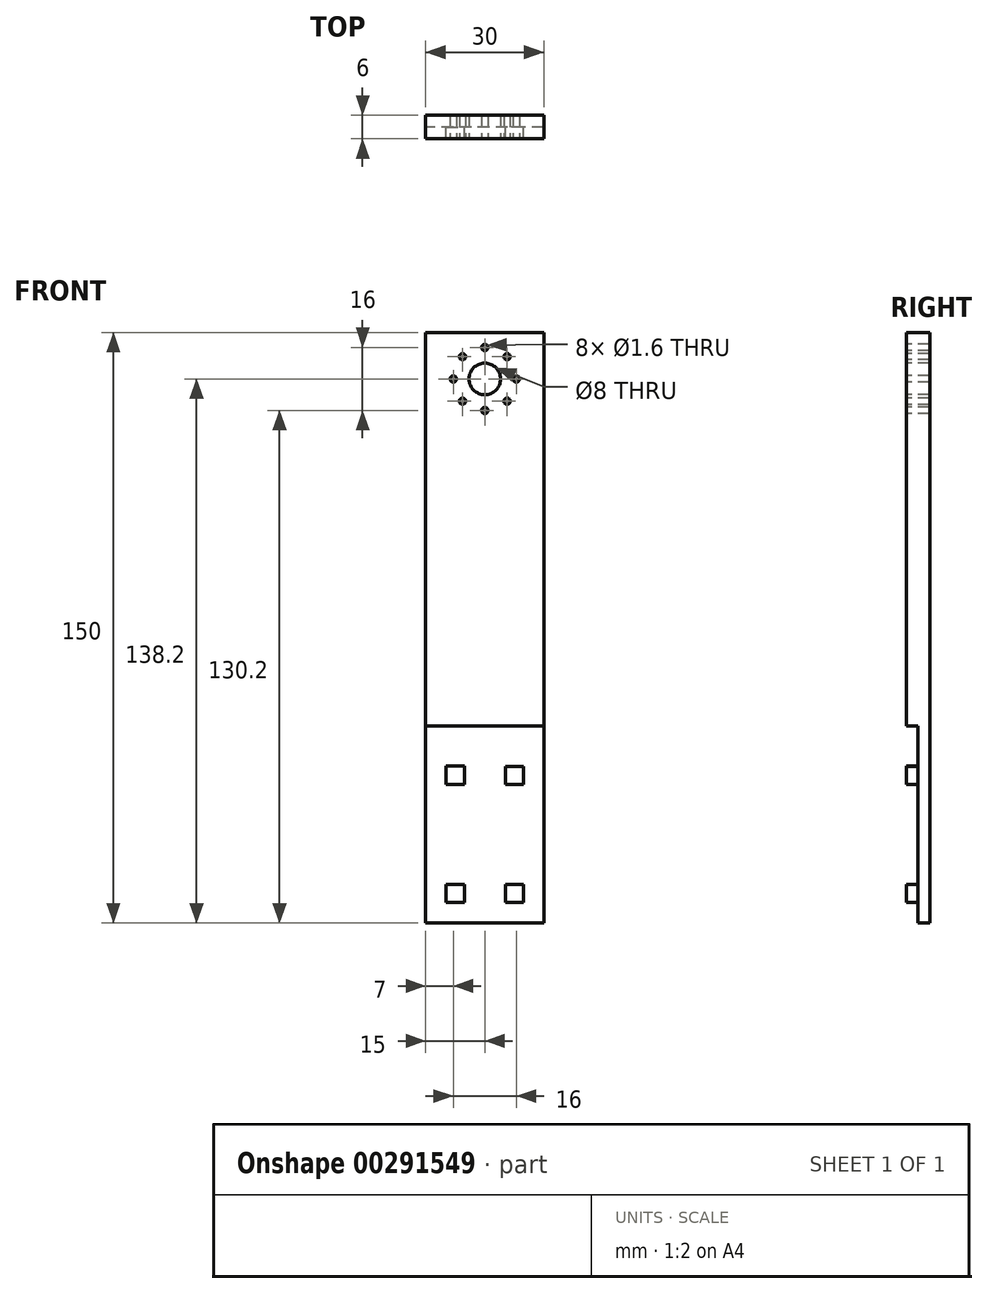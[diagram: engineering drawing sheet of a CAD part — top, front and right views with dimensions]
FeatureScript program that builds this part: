
annotation { "Feature Type Name" : "Feature", "Feature Type Description" : "" }
export const myFeature = defineFeature(function(context is Context, id is Id, definition is map)
    precondition{}
    {
        {
            var Q0;
            Q0=qCreatedBy(makeId("Top.planeOp"),FACE);
            var sketch = newSketch(context, id + "F0", { "sketchPlane" : qUnion([Q0])});
            skLineSegment(sketch, "E0.bottom", {"start": v(-15, 3) * mm, "end": v(15, 3) * mm});
            skLineSegment(sketch, "E0.top", {"start": v(-15, -3) * mm, "end": v(15, -3) * mm});
            skLineSegment(sketch, "E0.left", {"start": v(-15, 3) * mm, "end": v(-15, -3) * mm});
            skLineSegment(sketch, "E0.right", {"start": v(15, 3) * mm, "end": v(15, -3) * mm});
            skSolve(sketch);
        }
        {
            var Q0;
            Q0=qSketchRegion(id+"F0",true);
            extrude(context, id + "F1", {"entities" : qUnion([Q0]), "depth" : 150 * mm, "offsetDistance" : 25 * mm});
        }
        {
            var Q0;
            Q0=makeQuery(id+"F1.opExtrude","SWEPT_FACE",FACE,{"disambiguationData":[OSD([sQuery(id+"F0.wireOp",EDGE,"E0.top")])]});
            var sketch = newSketch(context, id + "F2", { "sketchPlane" : qUnion([Q0])});
            skCircle(sketch, "E1", {"center": v(0, 146.2) * mm, "radius": 0.8 * mm});
            skCircle(sketch, "E2", {"center": v(0, 138.2) * mm, "radius": 4 * mm});
            skCircle(sketch, "E3.1.0", {"center": v(-5.66, 143.86) * mm, "radius": 0.8 * mm});
            skCircle(sketch, "E3.2.0", {"center": v(-8, 138.2) * mm, "radius": 0.8 * mm});
            skCircle(sketch, "E3.3.0", {"center": v(-5.66, 132.54) * mm, "radius": 0.8 * mm});
            skCircle(sketch, "E3.4.0", {"center": v(0, 130.2) * mm, "radius": 0.8 * mm});
            skCircle(sketch, "E3.5.0", {"center": v(5.66, 132.54) * mm, "radius": 0.8 * mm});
            skCircle(sketch, "E3.6.0", {"center": v(8, 138.2) * mm, "radius": 0.8 * mm});
            skCircle(sketch, "E3.7.0", {"center": v(5.66, 143.86) * mm, "radius": 0.8 * mm});
            skSolve(sketch);
        }
        {
            var Q0;
            Q0=qSketchRegion(id+"F2",true);
            extrude(context, id + "F3", {"entities" : qUnion([Q0]), "operationType" : NewBodyOperationType.REMOVE, "endBound" : BoundingType.UP_TO_NEXT, "oppositeDirection" : true, "depth" : 25 * mm});
        }
        {
            var Q0;
            Q0=makeQuery(id+"F1.opExtrude","SWEPT_FACE",FACE,{"disambiguationData":[OSD([sQuery(id+"F0.wireOp",EDGE,"E0.left")])]});
            var sketch = newSketch(context, id + "F4", { "sketchPlane" : qUnion([Q0])});
            skLineSegment(sketch, "E4.bottom", {"start": v(0, 50) * mm, "end": v(3, 50) * mm});
            skLineSegment(sketch, "E4.top", {"start": v(0, 0) * mm, "end": v(3, 0) * mm});
            skLineSegment(sketch, "E4.left", {"start": v(0, 50) * mm, "end": v(0, 0) * mm});
            skLineSegment(sketch, "E4.right", {"start": v(3, 50) * mm, "end": v(3, 0) * mm});
            skSolve(sketch);
        }
        {
            var Q0;
            Q0=makeQuery(id+"F4.imprint","IMPRINT",FACE,{"disambiguationData":[TD([[makeQuery(id+"F4.imprint","IMPRINT",EDGE,{"derivedFrom":sQuery(id+"F4.wireOp",EDGE,"E4.bottom")}),-1.0]])]});
            extrude(context, id + "F5", {"entities" : qUnion([Q0]), "operationType" : NewBodyOperationType.REMOVE, "endBound" : BoundingType.UP_TO_NEXT, "oppositeDirection" : true, "depth" : 25 * mm, "offsetDistance" : 25 * mm});
        }
        {
            var Q0;
            Q0=makeQuery(id+"F5.boolean.opBoolean","COPY",FACE,{"derivedFrom":makeQuery(id+"F5.opExtrude","SWEPT_FACE",FACE,{"disambiguationData":[OSD([sQuery(id+"F4.wireOp",EDGE,"E4.left")])]})});
            var sketch = newSketch(context, id + "F6", { "sketchPlane" : qUnion([Q0])});
            skLineSegment(sketch, "E5.0", {"start": v(-9.8, 39.8) * mm, "end": v(-5.2, 39.8) * mm});
            skLineSegment(sketch, "E5.1", {"start": v(-9.8, 39.8) * mm, "end": v(-9.8, 35.2) * mm});
            skLineSegment(sketch, "E5.2", {"start": v(-9.8, 35.2) * mm, "end": v(-5.2, 35.2) * mm});
            skLineSegment(sketch, "E5.3", {"start": v(-5.2, 39.8) * mm, "end": v(-5.2, 35.2) * mm});
            skLineSegment(sketch, "E6.0", {"start": v(9.8, 39.8) * mm, "end": v(5.2, 39.8) * mm});
            skLineSegment(sketch, "E6.1", {"start": v(9.8, 39.8) * mm, "end": v(9.8, 35.2) * mm});
            skLineSegment(sketch, "E6.2", {"start": v(9.8, 35.2) * mm, "end": v(5.2, 35.2) * mm});
            skLineSegment(sketch, "E6.3", {"start": v(5.2, 39.8) * mm, "end": v(5.2, 35.2) * mm});
            skLineSegment(sketch, "E7.0", {"start": v(-9.8, 9.8) * mm, "end": v(-5.2, 9.8) * mm});
            skLineSegment(sketch, "E7.1", {"start": v(-9.8, 5.2) * mm, "end": v(-9.8, 9.8) * mm});
            skLineSegment(sketch, "E7.2", {"start": v(-9.8, 5.2) * mm, "end": v(-5.2, 5.2) * mm});
            skLineSegment(sketch, "E7.3", {"start": v(-5.2, 5.2) * mm, "end": v(-5.2, 9.8) * mm});
            skLineSegment(sketch, "E8.0", {"start": v(9.8, 9.8) * mm, "end": v(5.2, 9.8) * mm});
            skLineSegment(sketch, "E8.1", {"start": v(9.8, 5.2) * mm, "end": v(9.8, 9.8) * mm});
            skLineSegment(sketch, "E8.2", {"start": v(9.8, 5.2) * mm, "end": v(5.2, 5.2) * mm});
            skLineSegment(sketch, "E8.3", {"start": v(5.2, 5.2) * mm, "end": v(5.2, 9.8) * mm});
            skSolve(sketch);
        }
        {
            var Q0;
            Q0 = qSketchRegion(id + "F6", true);
            extrude(context, id + "F7", {"entities" : qUnion([Q0]), "operationType" : NewBodyOperationType.ADD, "depth" : 3 * mm, "offsetDistance" : 25 * mm});
        }
    });
